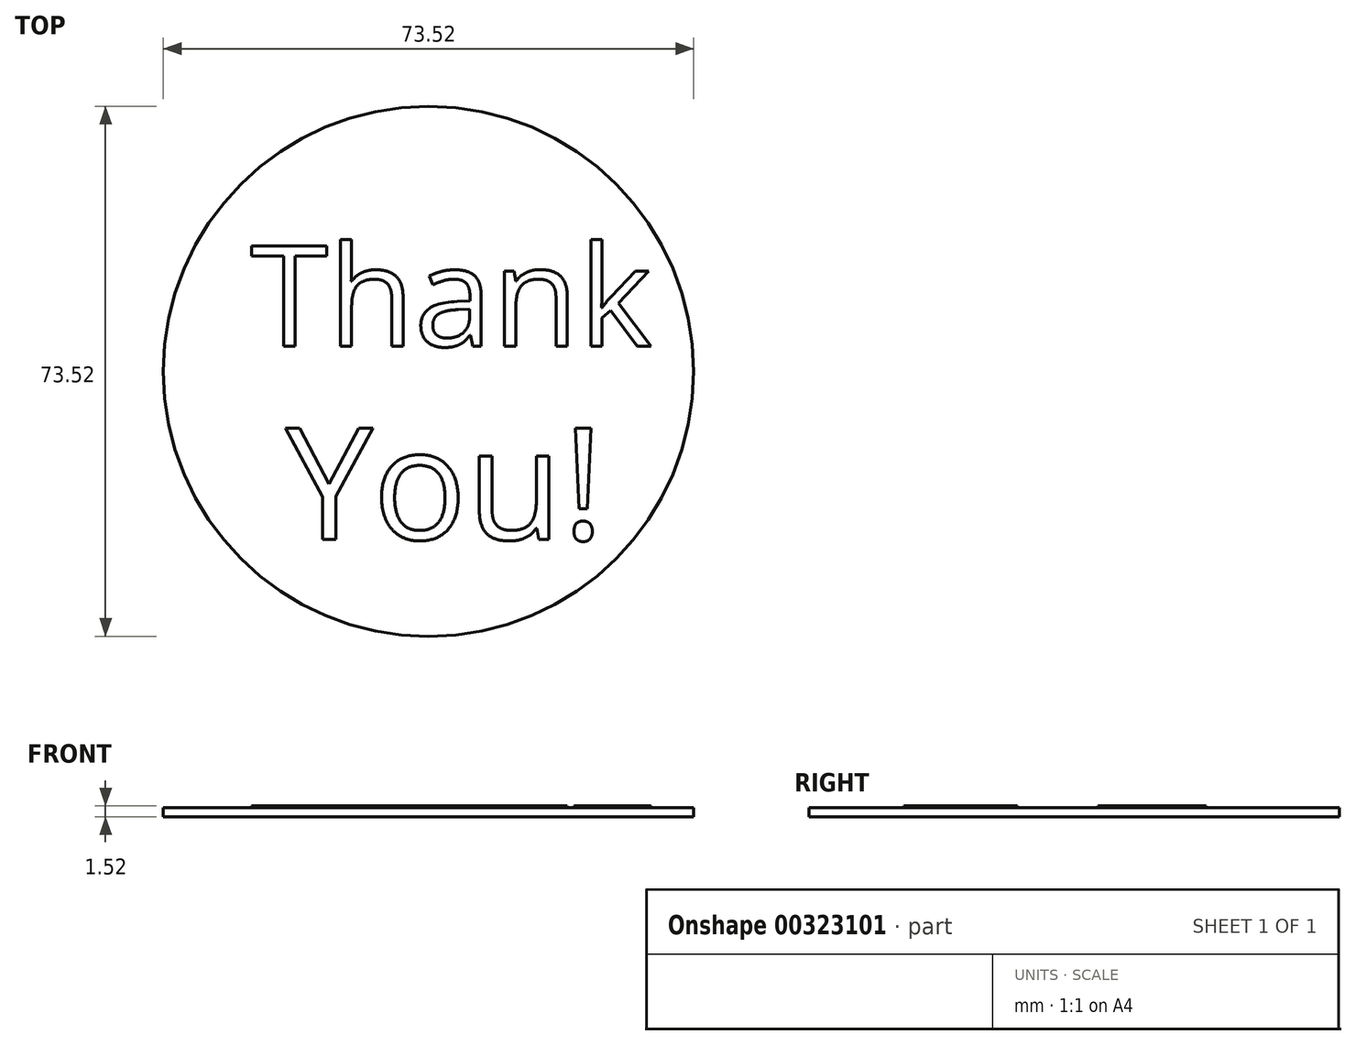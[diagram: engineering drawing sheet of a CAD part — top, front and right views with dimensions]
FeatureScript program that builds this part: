
annotation { "Feature Type Name" : "Feature", "Feature Type Description" : "" }
export const myFeature = defineFeature(function(context is Context, id is Id, definition is map)
    precondition{}
    {
        {
            var Q0;
            Q0=qCreatedBy(makeId("Top.planeOp"),FACE);
            var sketch = newSketch(context, id + "F0", { "sketchPlane" : qUnion([Q0])});
            skCircle(sketch, "E0", {"center": v(0, 0) * mm, "radius": 36.76 * mm});
            skSolve(sketch);
        }
        {
            var Q0;
            Q0 = qSketchRegion(id + "F0", true);
            extrude(context, id + "F1", {"entities" : qUnion([Q0]), "depth" : 1.27 * mm});
        }
        {
            var Q0;
            Q0=qCreatedBy(makeId("Top.planeOp"),FACE);
            var sketch = newSketch(context, id + "F2", { "sketchPlane" : qUnion([Q0])});
            skText(sketch, "E1", { "text": "Thank", "fontName": "OpenSans-Regular.ttf"});
            const initialGuessF2  = {"E1": [-0.03197, 0, 1, 0, 0.01585]};
            skSetInitialGuess(sketch, initialGuessF2);
            skSolve(sketch);
        }
        {
            var Q0;
            Q0 = qSketchRegion(id + "F2", true);
            extrude(context, id + "F3", {"entities" : qUnion([Q0]), "operationType" : NewBodyOperationType.ADD, "depth" : 0.25 * mm});
        }
        {
            var Q0;
            Q0=makeQuery(id+"F1.opExtrude","CAP_FACE",FACE,{"disambiguationData":[OSD([sQuery(id+"F0.wireOp",EDGE,"E0")])],"isStart":false});
            var sketch = newSketch(context, id + "F4", { "sketchPlane" : qUnion([Q0])});
            skText(sketch, "E2", { "text": "Thank", "fontName": "OpenSans-Regular.ttf"});
            const initialGuessF4  = {"E2": [-0.02469, 0.0035, 1, 0, 0.01402]};
            skSetInitialGuess(sketch, initialGuessF4);
            skSolve(sketch);
        }
        {
            var Q0;
            Q0 = qSketchRegion(id + "F4", true);
            extrude(context, id + "F5", {"entities" : qUnion([Q0]), "operationType" : NewBodyOperationType.ADD, "depth" : 0.25 * mm});
        }
        {
            var Q0;
            {var subQ0=sQuery(id+"F0.wireOp",EDGE,"E0");Q0=makeQuery(id+"F5.boolean.opBoolean","SPLIT",FACE,{"disambiguationData":[TD([makeQuery(id+"F1.opExtrude","SWEPT_FACE",FACE,{"disambiguationData":[OSD([subQ0])]})])],"derivedFrom":makeQuery(id+"F1.opExtrude","CAP_FACE",FACE,{"disambiguationData":[OSD([subQ0])],"isStart":false})});}
            var sketch = newSketch(context, id + "F6", { "sketchPlane" : qUnion([Q0])});
            skText(sketch, "E3", { "text": "You!", "fontName": "OpenSans-Regular.ttf"});
            const initialGuessF6  = {"E3": [-0.01981, -0.02332, 1, 0, 0.01554]};
            skSetInitialGuess(sketch, initialGuessF6);
            skSolve(sketch);
        }
        {
            var Q0;
            Q0 = qSketchRegion(id + "F6", true);
            extrude(context, id + "F7", {"entities" : qUnion([Q0]), "operationType" : NewBodyOperationType.ADD, "depth" : 0.25 * mm});
        }
    });
